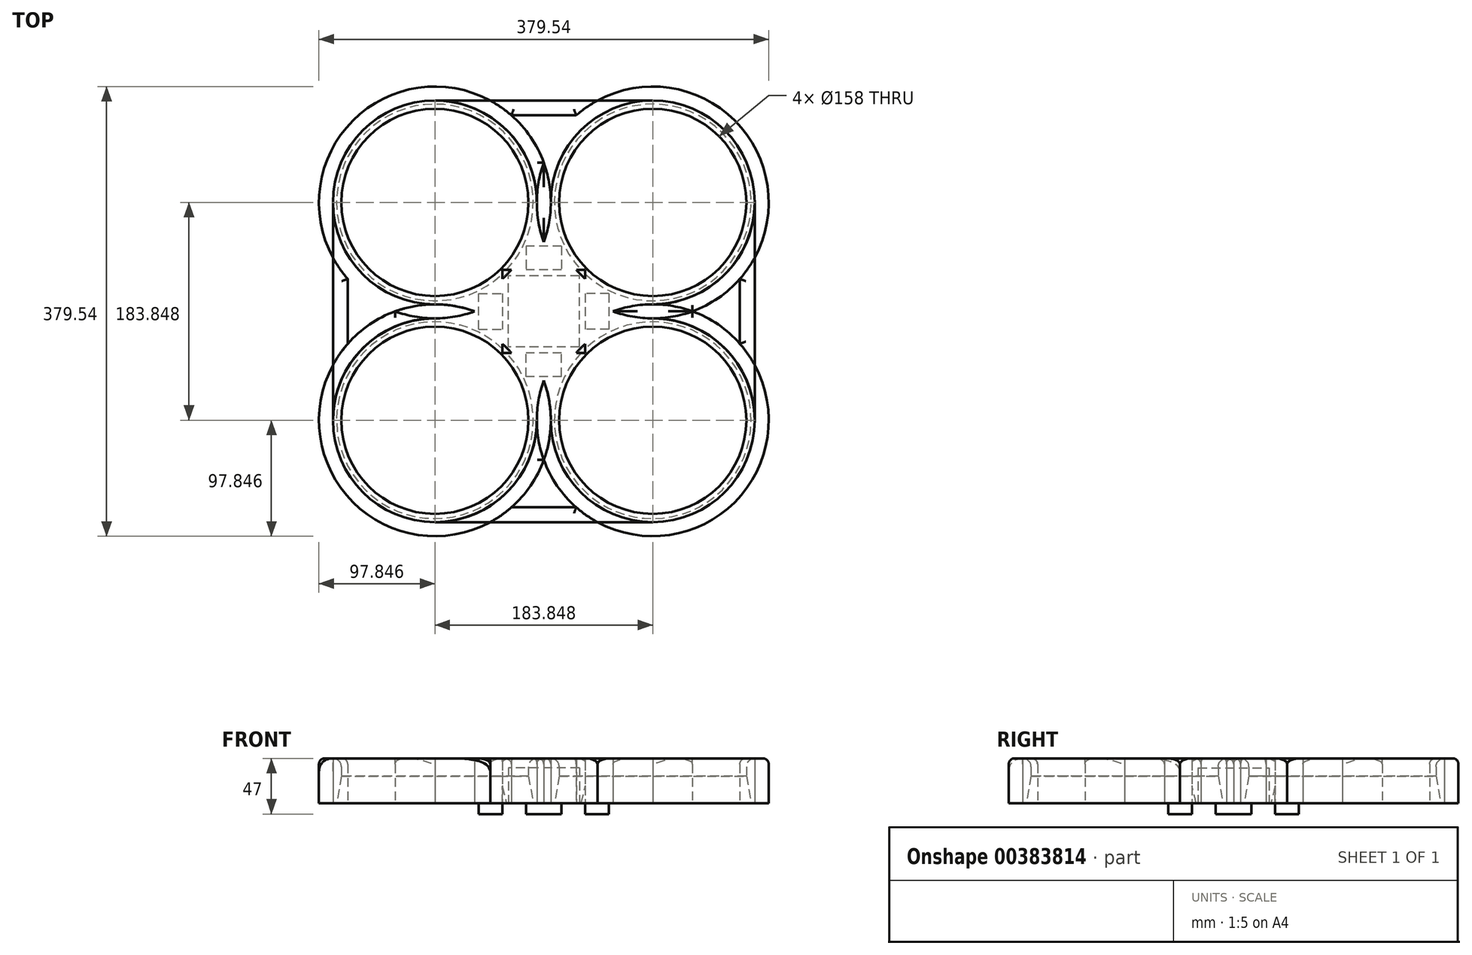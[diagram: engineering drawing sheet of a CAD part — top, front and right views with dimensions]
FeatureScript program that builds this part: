
annotation { "Feature Type Name" : "Feature", "Feature Type Description" : "" }
export const myFeature = defineFeature(function(context is Context, id is Id, definition is map)
    precondition{}
    {
        {
            var Q0;
            Q0=qCreatedBy(makeId("Top.planeOp"),FACE);
            var sketch = newSketch(context, id + "F0", { "sketchPlane" : qUnion([Q0])});
            skLineSegment(sketch, "E0.bottom", {"start": v(35, 35) * mm, "end": v(-35, 35) * mm});
            skLineSegment(sketch, "E0.top", {"start": v(35, -35) * mm, "end": v(-35, -35) * mm});
            skLineSegment(sketch, "E0.left", {"start": v(35, 35) * mm, "end": v(35, -35) * mm});
            skLineSegment(sketch, "E0.right", {"start": v(-35, 35) * mm, "end": v(-35, -35) * mm});
            skPoint(sketch, "E0.middle", {"position": v(0, 0) * mm});
            skLineSegment(sketch, "E1", {"start": v(0, 0) * mm, "end": v(91.92, 91.92) * mm, "construction": true});
            skLineSegment(sketch, "E2", {"start": v(0, 0) * mm, "end": v(-91.92, 91.92) * mm, "construction": true});
            skLineSegment(sketch, "E3", {"start": v(0, 0) * mm, "end": v(91.92, -91.92) * mm, "construction": true});
            skLineSegment(sketch, "E4", {"start": v(0, 0) * mm, "end": v(-91.92, -91.92) * mm, "construction": true});
            skCircle(sketch, "E5", {"center": v(-91.92, 91.92) * mm, "radius": 76.2 * mm, "construction": true});
            skCircle(sketch, "E6", {"center": v(-91.92, -91.92) * mm, "radius": 76.2 * mm, "construction": true});
            skCircle(sketch, "E7", {"center": v(91.92, -91.92) * mm, "radius": 76.2 * mm, "construction": true});
            skCircle(sketch, "E8", {"center": v(91.92, 91.92) * mm, "radius": 76.2 * mm, "construction": true});
            skCircle(sketch, "E9", {"center": v(-91.92, 91.92) * mm, "radius": 79 * mm});
            skCircle(sketch, "E10", {"center": v(91.92, 91.92) * mm, "radius": 79 * mm});
            skCircle(sketch, "E11", {"center": v(91.92, -91.92) * mm, "radius": 79 * mm});
            skCircle(sketch, "E12", {"center": v(-91.92, -91.92) * mm, "radius": 79 * mm});
            skCircle(sketch, "E13", {"center": v(91.92, -91.92) * mm, "radius": 86 * mm});
            skCircle(sketch, "E14", {"center": v(-91.92, -91.92) * mm, "radius": 86 * mm});
            skCircle(sketch, "E15", {"center": v(91.92, 91.92) * mm, "radius": 86 * mm});
            skCircle(sketch, "E16", {"center": v(-91.92, 91.92) * mm, "radius": 86 * mm});
            skLineSegment(sketch, "E17", {"start": v(-91.92, 91.92) * mm, "end": v(-177.92, 91.92) * mm, "construction": true});
            skLineSegment(sketch, "E18", {"start": v(-177.92, 91.92) * mm, "end": v(-177.92, -91.92) * mm});
            skLineSegment(sketch, "E19", {"start": v(-91.92, -91.92) * mm, "end": v(-91.92, -177.92) * mm, "construction": true});
            skLineSegment(sketch, "E20", {"start": v(-91.92, -177.92) * mm, "end": v(91.92, -177.92) * mm});
            skLineSegment(sketch, "E21", {"start": v(91.92, -91.92) * mm, "end": v(177.92, -91.92) * mm, "construction": true});
            skLineSegment(sketch, "E22", {"start": v(177.92, -91.92) * mm, "end": v(177.92, 91.92) * mm});
            skLineSegment(sketch, "E23", {"start": v(91.92, 91.92) * mm, "end": v(91.92, 177.92) * mm, "construction": true});
            skLineSegment(sketch, "E24", {"start": v(91.92, 177.92) * mm, "end": v(-91.92, 177.92) * mm});
            skCircle(sketch, "E25", {"center": v(-91.92, -91.92) * mm, "radius": 97.85 * mm});
            skCircle(sketch, "E26", {"center": v(-91.92, 91.92) * mm, "radius": 97.85 * mm});
            skLineSegment(sketch, "E27", {"start": v(0, 0) * mm, "end": v(-125.45, 0) * mm, "construction": true});
            skLineSegment(sketch, "E28", {"start": v(-125.45, 0) * mm, "end": v(-165.45, 0) * mm, "construction": true});
            skLineSegment(sketch, "E29", {"start": v(-165.45, 0) * mm, "end": v(-165.45, 27.37) * mm});
            skLineSegment(sketch, "E30", {"start": v(-165.45, 27.37) * mm, "end": v(-165.45, -27.37) * mm});
            skCircle(sketch, "E31", {"center": v(91.92, -91.92) * mm, "radius": 97.85 * mm});
            skCircle(sketch, "E32", {"center": v(91.92, 91.92) * mm, "radius": 97.85 * mm});
            skLineSegment(sketch, "E33", {"start": v(0, 0) * mm, "end": v(0, 125.45) * mm, "construction": true});
            skLineSegment(sketch, "E34", {"start": v(0, 125.45) * mm, "end": v(0, 165.45) * mm, "construction": true});
            skLineSegment(sketch, "E35", {"start": v(0, 165.45) * mm, "end": v(27.37, 165.45) * mm});
            skLineSegment(sketch, "E36", {"start": v(27.37, 165.45) * mm, "end": v(-27.37, 165.45) * mm});
            skLineSegment(sketch, "E37", {"start": v(0, 0) * mm, "end": v(0, -125.45) * mm, "construction": true});
            skLineSegment(sketch, "E38", {"start": v(0, -125.45) * mm, "end": v(0, -165.45) * mm, "construction": true});
            skLineSegment(sketch, "E39", {"start": v(0, -165.45) * mm, "end": v(27.37, -165.45) * mm});
            skLineSegment(sketch, "E40", {"start": v(27.37, -165.45) * mm, "end": v(-27.37, -165.45) * mm});
            skLineSegment(sketch, "E41", {"start": v(0, 0) * mm, "end": v(125.45, 0) * mm, "construction": true});
            skLineSegment(sketch, "E42", {"start": v(125.45, 0) * mm, "end": v(165.45, 0) * mm, "construction": true});
            skLineSegment(sketch, "E43", {"start": v(165.45, 0) * mm, "end": v(165.45, 27.37) * mm});
            skLineSegment(sketch, "E44", {"start": v(165.45, 27.37) * mm, "end": v(165.45, -27.37) * mm});
            skSolve(sketch);
        }
        {
            var Q0;
            {var subQ0=sQuery(id+"F0.wireOp",EDGE,"E20");var subQ1=sQuery(id+"F0.wireOp",EDGE,"E13");var subQ2=makeQuery(id+"F0.imprint","INTERSECT",VERTEX,{"derivedFrom":[subQ1,subQ0]});Q0=makeQuery(id+"F0.imprint","IMPRINT",FACE,{"disambiguationData":[TD([[makeQuery(id+"F0.imprint","IMPRINT",EDGE,{"disambiguationData":[TD([[subQ2,1.0]])],"derivedFrom":subQ1}),-1.0]])]});}
            var Q1;
            {var subQ0=sQuery(id+"F0.wireOp",EDGE,"E24");var subQ3=sQuery(id+"F0.wireOp",EDGE,"E26");var subQ5=makeQuery(id+"F0.imprint","INTERSECT",VERTEX,{"derivedFrom":[subQ0,subQ3]});Q1=makeQuery(id+"F0.imprint","IMPRINT",FACE,{"disambiguationData":[TD([[makeQuery(id+"F0.imprint","IMPRINT",EDGE,{"disambiguationData":[TD([[subQ5,1.0]])],"derivedFrom":subQ3}),-1.0]])]});}
            var Q2;
            {var subQ5=sQuery(id+"F0.wireOp",EDGE,"E22");Q2=makeQuery(id+"F0.imprint","IMPRINT",FACE,{"disambiguationData":[TD([[makeQuery(id+"F0.imprint","IMPRINT",EDGE,{"derivedFrom":subQ5}),1.0]])]});}
            var Q3;
            {var subQ4=sQuery(id+"F0.wireOp",EDGE,"E10");var subQ5=sQuery(id+"F0.wireOp",EDGE,"E1");var subQ6=makeQuery(id+"F0.imprint","INTERSECT",VERTEX,{"derivedFrom":[subQ5,subQ4]});Q3=makeQuery(id+"F0.imprint","IMPRINT",FACE,{"disambiguationData":[TD([[makeQuery(id+"F0.imprint","IMPRINT",EDGE,{"disambiguationData":[TD([[subQ6,-1.0]])],"derivedFrom":subQ4}),-1.0]])]});}
            var Q4;
            {var subQ0=sQuery(id+"F0.wireOp",EDGE,"E11");var subQ1=sQuery(id+"F0.wireOp",EDGE,"E3");var subQ2=makeQuery(id+"F0.imprint","INTERSECT",VERTEX,{"derivedFrom":[subQ1,subQ0]});Q4=makeQuery(id+"F0.imprint","IMPRINT",FACE,{"disambiguationData":[TD([[makeQuery(id+"F0.imprint","IMPRINT",EDGE,{"disambiguationData":[TD([[subQ2,1.0]])],"derivedFrom":subQ0}),-1.0]])]});}
            var Q5;
            {var subQ1=sQuery(id+"F0.wireOp",EDGE,"E26");var subQ3=sQuery(id+"F0.wireOp",EDGE,"E18");var subQ4=makeQuery(id+"F0.imprint","INTERSECT",VERTEX,{"derivedFrom":[subQ3,subQ1]});Q5=makeQuery(id+"F0.imprint","IMPRINT",FACE,{"disambiguationData":[TD([[makeQuery(id+"F0.imprint","IMPRINT",EDGE,{"disambiguationData":[TD([[subQ4,-1.0]])],"derivedFrom":subQ3}),1.0]])]});}
            var Q6;
            {var subQ4=sQuery(id+"F0.wireOp",EDGE,"E10");var subQ5=sQuery(id+"F0.wireOp",EDGE,"E1");var subQ6=makeQuery(id+"F0.imprint","INTERSECT",VERTEX,{"derivedFrom":[subQ5,subQ4]});Q6=makeQuery(id+"F0.imprint","IMPRINT",FACE,{"disambiguationData":[TD([[makeQuery(id+"F0.imprint","IMPRINT",EDGE,{"disambiguationData":[TD([[subQ6,1.0]])],"derivedFrom":subQ4}),-1.0]])]});}
            var Q7;
            {var subQ0=sQuery(id+"F0.wireOp",EDGE,"E26");var subQ6=sQuery(id+"F0.wireOp",EDGE,"E0.bottom");var subQ8=makeQuery(id+"F0.imprint","INTERSECT",VERTEX,{"derivedFrom":[subQ6,subQ0]});Q7=makeQuery(id+"F0.imprint","IMPRINT",FACE,{"disambiguationData":[TD([[makeQuery(id+"F0.imprint","IMPRINT",EDGE,{"disambiguationData":[TD([[subQ8,-1.0]])],"derivedFrom":subQ6}),-1.0]])]});}
            var Q8;
            {var subQ4=sQuery(id+"F0.wireOp",EDGE,"E11");var subQ5=sQuery(id+"F0.wireOp",EDGE,"E3");var subQ6=makeQuery(id+"F0.imprint","INTERSECT",VERTEX,{"derivedFrom":[subQ5,subQ4]});Q8=makeQuery(id+"F0.imprint","IMPRINT",FACE,{"disambiguationData":[TD([[makeQuery(id+"F0.imprint","IMPRINT",EDGE,{"disambiguationData":[TD([[subQ6,-1.0]])],"derivedFrom":subQ4}),-1.0]])]});}
            var Q9;
            {var subQ0=sQuery(id+"F0.wireOp",EDGE,"E25");var subQ1=sQuery(id+"F0.wireOp",EDGE,"E0.top");var subQ2=makeQuery(id+"F0.imprint","INTERSECT",VERTEX,{"derivedFrom":[subQ1,subQ0]});Q9=makeQuery(id+"F0.imprint","IMPRINT",FACE,{"disambiguationData":[TD([[makeQuery(id+"F0.imprint","IMPRINT",EDGE,{"disambiguationData":[TD([[subQ2,-1.0]])],"derivedFrom":subQ1}),1.0]])]});}
            var Q10;
            {var subQ2=sQuery(id+"F0.wireOp",EDGE,"E18");var subQ4=sQuery(id+"F0.wireOp",EDGE,"E14");var subQ5=makeQuery(id+"F0.imprint","INTERSECT",VERTEX,{"derivedFrom":[subQ4,subQ2]});Q10=makeQuery(id+"F0.imprint","IMPRINT",FACE,{"disambiguationData":[TD([[makeQuery(id+"F0.imprint","IMPRINT",EDGE,{"disambiguationData":[TD([[subQ5,1.0]])],"derivedFrom":subQ4}),-1.0]])]});}
            var Q11;
            {var subQ0=sQuery(id+"F0.wireOp",EDGE,"E26");var subQ1=makeQuery(id+"F0.imprint","INTERSECT",VERTEX,{"derivedFrom":[subQ0,sQuery(id+"F0.wireOp",EDGE,"E30")]});Q11=makeQuery(id+"F0.imprint","IMPRINT",FACE,{"disambiguationData":[TD([[makeQuery(id+"F0.imprint","IMPRINT",EDGE,{"disambiguationData":[TD([[subQ1,1.0]])],"derivedFrom":subQ0}),1.0]])]});}
            var Q12;
            {var subQ4=sQuery(id+"F0.wireOp",EDGE,"E12");var subQ5=sQuery(id+"F0.wireOp",EDGE,"E4");var subQ6=makeQuery(id+"F0.imprint","INTERSECT",VERTEX,{"derivedFrom":[subQ5,subQ4]});Q12=makeQuery(id+"F0.imprint","IMPRINT",FACE,{"disambiguationData":[TD([[makeQuery(id+"F0.imprint","IMPRINT",EDGE,{"disambiguationData":[TD([[subQ6,-1.0]])],"derivedFrom":subQ4}),-1.0]])]});}
            var Q13;
            {var subQ0=sQuery(id+"F0.wireOp",EDGE,"E2");var subQ3=sQuery(id+"F0.wireOp",EDGE,"E9");var subQ4=makeQuery(id+"F0.imprint","INTERSECT",VERTEX,{"derivedFrom":[subQ0,subQ3]});Q13=makeQuery(id+"F0.imprint","IMPRINT",FACE,{"disambiguationData":[TD([[makeQuery(id+"F0.imprint","IMPRINT",EDGE,{"disambiguationData":[TD([[subQ4,-1.0]])],"derivedFrom":subQ3}),-1.0]])]});}
            var Q14;
            {var subQ4=sQuery(id+"F0.wireOp",EDGE,"E9");var subQ5=sQuery(id+"F0.wireOp",EDGE,"E2");var subQ6=makeQuery(id+"F0.imprint","INTERSECT",VERTEX,{"derivedFrom":[subQ5,subQ4]});Q14=makeQuery(id+"F0.imprint","IMPRINT",FACE,{"disambiguationData":[TD([[makeQuery(id+"F0.imprint","IMPRINT",EDGE,{"disambiguationData":[TD([[subQ6,1.0]])],"derivedFrom":subQ4}),-1.0]])]});}
            var Q15;
            {var subQ0=sQuery(id+"F0.wireOp",EDGE,"E25");var subQ1=makeQuery(id+"F0.imprint","INTERSECT",VERTEX,{"derivedFrom":[sQuery(id+"F0.wireOp",EDGE,"E16"),subQ0]});Q15=makeQuery(id+"F0.imprint","IMPRINT",FACE,{"disambiguationData":[TD([[makeQuery(id+"F0.imprint","IMPRINT",EDGE,{"disambiguationData":[TD([[subQ1,1.0]])],"derivedFrom":subQ0}),1.0]])]});}
            var Q16;
            {var subQ1=sQuery(id+"F0.wireOp",EDGE,"E26");var subQ4=makeQuery(id+"F0.imprint","INTERSECT",VERTEX,{"derivedFrom":[sQuery(id+"F0.wireOp",EDGE,"E14"),subQ1]});Q16=makeQuery(id+"F0.imprint","IMPRINT",FACE,{"disambiguationData":[TD([[makeQuery(id+"F0.imprint","IMPRINT",EDGE,{"disambiguationData":[TD([[subQ4,-1.0]])],"derivedFrom":subQ1}),1.0]])]});}
            var Q17;
            {var subQ0=sQuery(id+"F0.wireOp",EDGE,"E25");var subQ1=sQuery(id+"F0.wireOp",EDGE,"E0.right");var subQ2=makeQuery(id+"F0.imprint","INTERSECT",VERTEX,{"derivedFrom":[subQ1,subQ0]});Q17=makeQuery(id+"F0.imprint","IMPRINT",FACE,{"disambiguationData":[TD([[makeQuery(id+"F0.imprint","IMPRINT",EDGE,{"disambiguationData":[TD([[subQ2,-1.0]])],"derivedFrom":subQ1}),-1.0]])]});}
            var Q18;
            {var subQ0=sQuery(id+"F0.wireOp",EDGE,"E16");var subQ1=sQuery(id+"F0.wireOp",EDGE,"E0.right");var subQ2=makeQuery(id+"F0.imprint","INTERSECT",VERTEX,{"derivedFrom":[subQ1,subQ0]});Q18=makeQuery(id+"F0.imprint","IMPRINT",FACE,{"disambiguationData":[TD([[makeQuery(id+"F0.imprint","IMPRINT",EDGE,{"disambiguationData":[TD([[subQ2,-1.0]])],"derivedFrom":subQ1}),-1.0]])]});}
            var Q19;
            {var subQ1=sQuery(id+"F0.wireOp",EDGE,"E0.right");var subQ3=sQuery(id+"F0.wireOp",EDGE,"E16");var subQ4=makeQuery(id+"F0.imprint","INTERSECT",VERTEX,{"derivedFrom":[subQ1,subQ3]});Q19=makeQuery(id+"F0.imprint","IMPRINT",FACE,{"disambiguationData":[TD([[makeQuery(id+"F0.imprint","IMPRINT",EDGE,{"disambiguationData":[TD([[subQ4,-1.0]])],"derivedFrom":subQ3}),1.0]])]});}
            var Q20;
            {var subQ1=sQuery(id+"F0.wireOp",EDGE,"E0.bottom");var subQ3=sQuery(id+"F0.wireOp",EDGE,"E16");var subQ4=makeQuery(id+"F0.imprint","INTERSECT",VERTEX,{"derivedFrom":[subQ1,subQ3]});Q20=makeQuery(id+"F0.imprint","IMPRINT",FACE,{"disambiguationData":[TD([[makeQuery(id+"F0.imprint","IMPRINT",EDGE,{"disambiguationData":[TD([[subQ4,1.0]])],"derivedFrom":subQ3}),1.0]])]});}
            var Q21;
            {var subQ1=sQuery(id+"F0.wireOp",EDGE,"E0.right");var subQ3=sQuery(id+"F0.wireOp",EDGE,"E14");var subQ4=makeQuery(id+"F0.imprint","INTERSECT",VERTEX,{"derivedFrom":[subQ1,subQ3]});Q21=makeQuery(id+"F0.imprint","IMPRINT",FACE,{"disambiguationData":[TD([[makeQuery(id+"F0.imprint","IMPRINT",EDGE,{"disambiguationData":[TD([[subQ4,1.0]])],"derivedFrom":subQ3}),1.0]])]});}
            var Q22;
            {var subQ0=sQuery(id+"F0.wireOp",EDGE,"E12");var subQ1=sQuery(id+"F0.wireOp",EDGE,"E4");var subQ2=makeQuery(id+"F0.imprint","INTERSECT",VERTEX,{"derivedFrom":[subQ1,subQ0]});Q22=makeQuery(id+"F0.imprint","IMPRINT",FACE,{"disambiguationData":[TD([[makeQuery(id+"F0.imprint","IMPRINT",EDGE,{"disambiguationData":[TD([[subQ2,1.0]])],"derivedFrom":subQ0}),-1.0]])]});}
            var Q23;
            {var subQ0=sQuery(id+"F0.wireOp",EDGE,"E26");var subQ1=sQuery(id+"F0.wireOp",EDGE,"E0.right");var subQ2=makeQuery(id+"F0.imprint","INTERSECT",VERTEX,{"derivedFrom":[subQ1,subQ0]});Q23=makeQuery(id+"F0.imprint","IMPRINT",FACE,{"disambiguationData":[TD([[makeQuery(id+"F0.imprint","IMPRINT",EDGE,{"disambiguationData":[TD([[subQ2,-1.0]])],"derivedFrom":subQ1}),-1.0]])]});}
            var Q24;
            {var subQ0=sQuery(id+"F0.wireOp",EDGE,"E27");var subQ1=sQuery(id+"F0.wireOp",EDGE,"E0.right");var subQ2=makeQuery(id+"F0.imprint","INTERSECT",VERTEX,{"derivedFrom":[subQ1,subQ0]});Q24=makeQuery(id+"F0.imprint","IMPRINT",FACE,{"disambiguationData":[TD([[makeQuery(id+"F0.imprint","IMPRINT",EDGE,{"disambiguationData":[TD([[subQ2,-1.0]])],"derivedFrom":subQ1}),-1.0]])]});}
            var Q25;
            {var subQ0=sQuery(id+"F0.wireOp",EDGE,"E13");var subQ1=sQuery(id+"F0.wireOp",EDGE,"E0.top");var subQ2=makeQuery(id+"F0.imprint","INTERSECT",VERTEX,{"derivedFrom":[subQ1,subQ0]});Q25=makeQuery(id+"F0.imprint","IMPRINT",FACE,{"disambiguationData":[TD([[makeQuery(id+"F0.imprint","IMPRINT",EDGE,{"disambiguationData":[TD([[subQ2,-1.0]])],"derivedFrom":subQ1}),1.0]])]});}
            var Q26;
            {var subQ0=sQuery(id+"F0.wireOp",EDGE,"E15");var subQ1=sQuery(id+"F0.wireOp",EDGE,"E0.bottom");var subQ2=makeQuery(id+"F0.imprint","INTERSECT",VERTEX,{"derivedFrom":[subQ1,subQ0]});Q26=makeQuery(id+"F0.imprint","IMPRINT",FACE,{"disambiguationData":[TD([[makeQuery(id+"F0.imprint","IMPRINT",EDGE,{"disambiguationData":[TD([[subQ2,-1.0]])],"derivedFrom":subQ1}),-1.0]])]});}
            var Q27;
            {var subQ0=sQuery(id+"F0.wireOp",EDGE,"E25");var subQ1=makeQuery(id+"F0.imprint","INTERSECT",VERTEX,{"derivedFrom":[sQuery(id+"F0.wireOp",EDGE,"E13"),subQ0]});Q27=makeQuery(id+"F0.imprint","IMPRINT",FACE,{"disambiguationData":[TD([[makeQuery(id+"F0.imprint","IMPRINT",EDGE,{"disambiguationData":[TD([[subQ1,-1.0]])],"derivedFrom":subQ0}),1.0]])]});}
            var Q28;
            {var subQ0=sQuery(id+"F0.wireOp",EDGE,"E31");var subQ1=makeQuery(id+"F0.imprint","INTERSECT",VERTEX,{"derivedFrom":[sQuery(id+"F0.wireOp",EDGE,"E14"),subQ0]});Q28=makeQuery(id+"F0.imprint","IMPRINT",FACE,{"disambiguationData":[TD([[makeQuery(id+"F0.imprint","IMPRINT",EDGE,{"disambiguationData":[TD([[subQ1,1.0]])],"derivedFrom":subQ0}),1.0]])]});}
            var Q29;
            {var subQ0=sQuery(id+"F0.wireOp",EDGE,"E25");var subQ1=makeQuery(id+"F0.imprint","INTERSECT",VERTEX,{"derivedFrom":[subQ0,sQuery(id+"F0.wireOp",EDGE,"E40")]});Q29=makeQuery(id+"F0.imprint","IMPRINT",FACE,{"disambiguationData":[TD([[makeQuery(id+"F0.imprint","IMPRINT",EDGE,{"disambiguationData":[TD([[subQ1,1.0]])],"derivedFrom":subQ0}),1.0]])]});}
            var Q30;
            {var subQ4=sQuery(id+"F0.wireOp",EDGE,"E20");var subQ6=sQuery(id+"F0.wireOp",EDGE,"E25");var subQ8=makeQuery(id+"F0.imprint","INTERSECT",VERTEX,{"derivedFrom":[subQ4,subQ6]});Q30=makeQuery(id+"F0.imprint","IMPRINT",FACE,{"disambiguationData":[TD([[makeQuery(id+"F0.imprint","IMPRINT",EDGE,{"disambiguationData":[TD([[subQ8,-1.0]])],"derivedFrom":subQ4}),1.0]])]});}
            var Q31;
            {var subQ2=sQuery(id+"F0.wireOp",EDGE,"E24");var subQ6=sQuery(id+"F0.wireOp",EDGE,"E16");var subQ8=makeQuery(id+"F0.imprint","INTERSECT",VERTEX,{"derivedFrom":[subQ6,subQ2]});Q31=makeQuery(id+"F0.imprint","IMPRINT",FACE,{"disambiguationData":[TD([[makeQuery(id+"F0.imprint","IMPRINT",EDGE,{"disambiguationData":[TD([[subQ8,1.0]])],"derivedFrom":subQ6}),-1.0]])]});}
            var Q32;
            {var subQ0=sQuery(id+"F0.wireOp",EDGE,"E32");var subQ1=makeQuery(id+"F0.imprint","INTERSECT",VERTEX,{"derivedFrom":[subQ0,sQuery(id+"F0.wireOp",EDGE,"E36")]});Q32=makeQuery(id+"F0.imprint","IMPRINT",FACE,{"disambiguationData":[TD([[makeQuery(id+"F0.imprint","IMPRINT",EDGE,{"disambiguationData":[TD([[subQ1,1.0]])],"derivedFrom":subQ0}),1.0]])]});}
            var Q33;
            {var subQ1=sQuery(id+"F0.wireOp",EDGE,"E32");var subQ4=makeQuery(id+"F0.imprint","INTERSECT",VERTEX,{"derivedFrom":[sQuery(id+"F0.wireOp",EDGE,"E16"),subQ1]});Q33=makeQuery(id+"F0.imprint","IMPRINT",FACE,{"disambiguationData":[TD([[makeQuery(id+"F0.imprint","IMPRINT",EDGE,{"disambiguationData":[TD([[subQ4,-1.0]])],"derivedFrom":subQ1}),1.0]])]});}
            var Q34;
            {var subQ2=sQuery(id+"F0.wireOp",EDGE,"E26");var subQ4=makeQuery(id+"F0.imprint","INTERSECT",VERTEX,{"derivedFrom":[sQuery(id+"F0.wireOp",EDGE,"E15"),subQ2]});Q34=makeQuery(id+"F0.imprint","IMPRINT",FACE,{"disambiguationData":[TD([[makeQuery(id+"F0.imprint","IMPRINT",EDGE,{"disambiguationData":[TD([[subQ4,1.0]])],"derivedFrom":subQ2}),1.0]])]});}
            var Q35;
            {var subQ0=sQuery(id+"F0.wireOp",EDGE,"E15");var subQ1=sQuery(id+"F0.wireOp",EDGE,"E0.left");var subQ2=makeQuery(id+"F0.imprint","INTERSECT",VERTEX,{"derivedFrom":[subQ1,subQ0]});Q35=makeQuery(id+"F0.imprint","IMPRINT",FACE,{"disambiguationData":[TD([[makeQuery(id+"F0.imprint","IMPRINT",EDGE,{"disambiguationData":[TD([[subQ2,-1.0]])],"derivedFrom":subQ1}),1.0]])]});}
            var Q36;
            {var subQ0=sQuery(id+"F0.wireOp",EDGE,"E32");var subQ1=makeQuery(id+"F0.imprint","INTERSECT",VERTEX,{"derivedFrom":[sQuery(id+"F0.wireOp",EDGE,"E13"),subQ0]});Q36=makeQuery(id+"F0.imprint","IMPRINT",FACE,{"disambiguationData":[TD([[makeQuery(id+"F0.imprint","IMPRINT",EDGE,{"disambiguationData":[TD([[subQ1,1.0]])],"derivedFrom":subQ0}),1.0]])]});}
            var Q37;
            {var subQ2=sQuery(id+"F0.wireOp",EDGE,"E31");var subQ4=makeQuery(id+"F0.imprint","INTERSECT",VERTEX,{"derivedFrom":[sQuery(id+"F0.wireOp",EDGE,"E15"),subQ2]});Q37=makeQuery(id+"F0.imprint","IMPRINT",FACE,{"disambiguationData":[TD([[makeQuery(id+"F0.imprint","IMPRINT",EDGE,{"disambiguationData":[TD([[subQ4,-1.0]])],"derivedFrom":subQ2}),1.0]])]});}
            var Q38;
            {var subQ0=sQuery(id+"F0.wireOp",EDGE,"E31");var subQ1=sQuery(id+"F0.wireOp",EDGE,"E0.left");var subQ2=makeQuery(id+"F0.imprint","INTERSECT",VERTEX,{"derivedFrom":[subQ1,subQ0]});Q38=makeQuery(id+"F0.imprint","IMPRINT",FACE,{"disambiguationData":[TD([[makeQuery(id+"F0.imprint","IMPRINT",EDGE,{"disambiguationData":[TD([[subQ2,-1.0]])],"derivedFrom":subQ1}),1.0]])]});}
            var Q39;
            {var subQ1=sQuery(id+"F0.wireOp",EDGE,"E0.top");var subQ3=sQuery(id+"F0.wireOp",EDGE,"E14");var subQ4=makeQuery(id+"F0.imprint","INTERSECT",VERTEX,{"derivedFrom":[subQ1,subQ3]});Q39=makeQuery(id+"F0.imprint","IMPRINT",FACE,{"disambiguationData":[TD([[makeQuery(id+"F0.imprint","IMPRINT",EDGE,{"disambiguationData":[TD([[subQ4,-1.0]])],"derivedFrom":subQ3}),1.0]])]});}
            var Q40;
            {var subQ0=sQuery(id+"F0.wireOp",EDGE,"E32");var subQ1=sQuery(id+"F0.wireOp",EDGE,"E0.bottom");var subQ2=makeQuery(id+"F0.imprint","INTERSECT",VERTEX,{"derivedFrom":[subQ1,subQ0]});Q40=makeQuery(id+"F0.imprint","IMPRINT",FACE,{"disambiguationData":[TD([[makeQuery(id+"F0.imprint","IMPRINT",EDGE,{"disambiguationData":[TD([[subQ2,-1.0]])],"derivedFrom":subQ1}),-1.0]])]});}
            var Q41;
            {var subQ0=sQuery(id+"F0.wireOp",EDGE,"E33");var subQ1=sQuery(id+"F0.wireOp",EDGE,"E0.bottom");var subQ2=makeQuery(id+"F0.imprint","INTERSECT",VERTEX,{"derivedFrom":[subQ1,subQ0]});Q41=makeQuery(id+"F0.imprint","IMPRINT",FACE,{"disambiguationData":[TD([[makeQuery(id+"F0.imprint","IMPRINT",EDGE,{"disambiguationData":[TD([[subQ2,-1.0]])],"derivedFrom":subQ1}),-1.0]])]});}
            var Q42;
            {var subQ0=sQuery(id+"F0.wireOp",EDGE,"E41");var subQ1=sQuery(id+"F0.wireOp",EDGE,"E0.left");var subQ2=makeQuery(id+"F0.imprint","INTERSECT",VERTEX,{"derivedFrom":[subQ1,subQ0]});Q42=makeQuery(id+"F0.imprint","IMPRINT",FACE,{"disambiguationData":[TD([[makeQuery(id+"F0.imprint","IMPRINT",EDGE,{"disambiguationData":[TD([[subQ2,-1.0]])],"derivedFrom":subQ1}),1.0]])]});}
            var Q43;
            {var subQ0=sQuery(id+"F0.wireOp",EDGE,"E32");var subQ1=sQuery(id+"F0.wireOp",EDGE,"E0.left");var subQ2=makeQuery(id+"F0.imprint","INTERSECT",VERTEX,{"derivedFrom":[subQ1,subQ0]});Q43=makeQuery(id+"F0.imprint","IMPRINT",FACE,{"disambiguationData":[TD([[makeQuery(id+"F0.imprint","IMPRINT",EDGE,{"disambiguationData":[TD([[subQ2,-1.0]])],"derivedFrom":subQ1}),1.0]])]});}
            var Q44;
            Q44=makeQuery(id+"F0.imprint","IMPRINT",FACE,{"disambiguationData":[TD([[makeQuery(id+"F0.imprint","IMPRINT",EDGE,{"derivedFrom":sQuery(id+"F0.wireOp",EDGE,"E12")}),-1.0]])]});
            var Q45;
            Q45=makeQuery(id+"F0.imprint","IMPRINT",FACE,{"disambiguationData":[TD([[makeQuery(id+"F0.imprint","IMPRINT",EDGE,{"derivedFrom":sQuery(id+"F0.wireOp",EDGE,"E11")}),-1.0]])]});
            var Q46;
            Q46=makeQuery(id+"F0.imprint","IMPRINT",FACE,{"disambiguationData":[TD([[makeQuery(id+"F0.imprint","IMPRINT",EDGE,{"derivedFrom":sQuery(id+"F0.wireOp",EDGE,"E10")}),-1.0]])]});
            var Q47;
            Q47=makeQuery(id+"F0.imprint","IMPRINT",FACE,{"disambiguationData":[TD([[makeQuery(id+"F0.imprint","IMPRINT",EDGE,{"derivedFrom":sQuery(id+"F0.wireOp",EDGE,"E9")}),-1.0]])]});
            var Q48;
            {var subQ5=sQuery(id+"F0.wireOp",EDGE,"E32");var subQ13=sQuery(id+"F0.wireOp",EDGE,"E0.bottom");var subQ14=makeQuery(id+"F0.imprint","INTERSECT",VERTEX,{"derivedFrom":[subQ13,subQ5]});Q48=makeQuery(id+"F0.imprint","IMPRINT",FACE,{"disambiguationData":[TD([[makeQuery(id+"F0.imprint","IMPRINT",EDGE,{"disambiguationData":[TD([[subQ14,-1.0]])],"derivedFrom":subQ13}),1.0]])]});}
            var Q49;
            {var subQ0=sQuery(id+"F0.wireOp",EDGE,"E26");var subQ1=sQuery(id+"F0.wireOp",EDGE,"E0.bottom");var subQ2=makeQuery(id+"F0.imprint","INTERSECT",VERTEX,{"derivedFrom":[subQ1,subQ0]});Q49=makeQuery(id+"F0.imprint","IMPRINT",FACE,{"disambiguationData":[TD([[makeQuery(id+"F0.imprint","IMPRINT",EDGE,{"disambiguationData":[TD([[subQ2,-1.0]])],"derivedFrom":subQ1}),1.0]])]});}
            var Q50;
            {var subQ0=sQuery(id+"F0.wireOp",EDGE,"E15");var subQ1=sQuery(id+"F0.wireOp",EDGE,"E0.bottom");var subQ2=makeQuery(id+"F0.imprint","INTERSECT",VERTEX,{"derivedFrom":[subQ1,subQ0]});Q50=makeQuery(id+"F0.imprint","IMPRINT",FACE,{"disambiguationData":[TD([[makeQuery(id+"F0.imprint","IMPRINT",EDGE,{"disambiguationData":[TD([[subQ2,-1.0]])],"derivedFrom":subQ1}),1.0]])]});}
            var Q51;
            {var subQ0=sQuery(id+"F0.wireOp",EDGE,"E13");var subQ1=sQuery(id+"F0.wireOp",EDGE,"E0.top");var subQ2=makeQuery(id+"F0.imprint","INTERSECT",VERTEX,{"derivedFrom":[subQ1,subQ0]});Q51=makeQuery(id+"F0.imprint","IMPRINT",FACE,{"disambiguationData":[TD([[makeQuery(id+"F0.imprint","IMPRINT",EDGE,{"disambiguationData":[TD([[subQ2,-1.0]])],"derivedFrom":subQ1}),-1.0]])]});}
            var Q52;
            {var subQ0=sQuery(id+"F0.wireOp",EDGE,"E25");var subQ1=sQuery(id+"F0.wireOp",EDGE,"E0.top");var subQ2=makeQuery(id+"F0.imprint","INTERSECT",VERTEX,{"derivedFrom":[subQ1,subQ0]});Q52=makeQuery(id+"F0.imprint","IMPRINT",FACE,{"disambiguationData":[TD([[makeQuery(id+"F0.imprint","IMPRINT",EDGE,{"disambiguationData":[TD([[subQ2,-1.0]])],"derivedFrom":subQ1}),-1.0]])]});}
            var Q53;
            {var subQ0=sQuery(id+"F0.wireOp",EDGE,"E31");var subQ1=sQuery(id+"F0.wireOp",EDGE,"E0.top");var subQ2=makeQuery(id+"F0.imprint","INTERSECT",VERTEX,{"derivedFrom":[subQ1,subQ0]});Q53=makeQuery(id+"F0.imprint","IMPRINT",FACE,{"disambiguationData":[TD([[makeQuery(id+"F0.imprint","IMPRINT",EDGE,{"disambiguationData":[TD([[subQ2,-1.0]])],"derivedFrom":subQ1}),1.0]])]});}
            var Q54;
            {var subQ0=sQuery(id+"F0.wireOp",EDGE,"E0.left");var subQ1=sQuery(id+"F0.wireOp",EDGE,"E0.top");var subQ2=makeQuery(id+"F0.imprint","INTERSECT",VERTEX,{"derivedFrom":[subQ1,subQ0]});Q54=makeQuery(id+"F0.imprint","IMPRINT",FACE,{"disambiguationData":[TD([[makeQuery(id+"F0.imprint","IMPRINT",EDGE,{"disambiguationData":[TD([[subQ2,-1.0]])],"derivedFrom":subQ1}),-1.0]])]});}
            var Q55;
            {var subQ0=sQuery(id+"F0.wireOp",EDGE,"E0.left");var subQ1=sQuery(id+"F0.wireOp",EDGE,"E0.bottom");var subQ2=makeQuery(id+"F0.imprint","INTERSECT",VERTEX,{"derivedFrom":[subQ1,subQ0]});Q55=makeQuery(id+"F0.imprint","IMPRINT",FACE,{"disambiguationData":[TD([[makeQuery(id+"F0.imprint","IMPRINT",EDGE,{"disambiguationData":[TD([[subQ2,-1.0]])],"derivedFrom":subQ1}),1.0]])]});}
            var Q56;
            {var subQ0=sQuery(id+"F0.wireOp",EDGE,"E20");var subQ1=sQuery(id+"F0.wireOp",EDGE,"E13");var subQ2=makeQuery(id+"F0.imprint","INTERSECT",VERTEX,{"derivedFrom":[subQ1,subQ0]});Q56=makeQuery(id+"F0.imprint","IMPRINT",FACE,{"disambiguationData":[TD([[makeQuery(id+"F0.imprint","IMPRINT",EDGE,{"disambiguationData":[TD([[subQ2,-1.0]])],"derivedFrom":subQ1}),-1.0]])]});}
            var Q57;
            {var subQ0=sQuery(id+"F0.wireOp",EDGE,"E22");var subQ1=sQuery(id+"F0.wireOp",EDGE,"E15");var subQ2=makeQuery(id+"F0.imprint","INTERSECT",VERTEX,{"derivedFrom":[subQ1,subQ0]});Q57=makeQuery(id+"F0.imprint","IMPRINT",FACE,{"disambiguationData":[TD([[makeQuery(id+"F0.imprint","IMPRINT",EDGE,{"disambiguationData":[TD([[subQ2,-1.0]])],"derivedFrom":subQ1}),-1.0]])]});}
            var Q58;
            {var subQ0=sQuery(id+"F0.wireOp",EDGE,"E18");var subQ1=sQuery(id+"F0.wireOp",EDGE,"E16");var subQ2=makeQuery(id+"F0.imprint","INTERSECT",VERTEX,{"derivedFrom":[subQ1,subQ0]});Q58=makeQuery(id+"F0.imprint","IMPRINT",FACE,{"disambiguationData":[TD([[makeQuery(id+"F0.imprint","IMPRINT",EDGE,{"disambiguationData":[TD([[subQ2,1.0]])],"derivedFrom":subQ1}),-1.0]])]});}
            var Q59;
            {var subQ0=sQuery(id+"F0.wireOp",EDGE,"E18");var subQ1=sQuery(id+"F0.wireOp",EDGE,"E14");var subQ2=makeQuery(id+"F0.imprint","INTERSECT",VERTEX,{"derivedFrom":[subQ1,subQ0]});Q59=makeQuery(id+"F0.imprint","IMPRINT",FACE,{"disambiguationData":[TD([[makeQuery(id+"F0.imprint","IMPRINT",EDGE,{"disambiguationData":[TD([[subQ2,-1.0]])],"derivedFrom":subQ1}),-1.0]])]});}
            extrude(context, id + "F1", {"entities" : qUnion([Q0, Q1, Q2, Q3, Q4, Q5, Q6, Q7, Q8, Q9, Q10, Q11, Q12, Q13, Q14, Q15, Q16, Q17, Q18, Q19, Q20, Q21, Q22, Q23, Q24, Q25, Q26, Q27, Q28, Q29, Q30, Q31, Q32, Q33, Q34, Q35, Q36, Q37, Q38, Q39, Q40, Q41, Q42, Q43, Q44, Q45, Q46, Q47, Q48, Q49, Q50, Q51, Q52, Q53, Q54, Q55, Q56, Q57, Q58, Q59]), "depth" : 38 * mm});
        }
        {
            var Q0;
            Q0=makeQuery(id+"F1.opExtrude","CAP_EDGE",EDGE,{"disambiguationData":[OSD([sQuery(id+"F0.wireOp",EDGE,"E12")])],"isStart":false});
            var Q1;
            Q1=makeQuery(id+"F1.opExtrude","CAP_EDGE",EDGE,{"disambiguationData":[OSD([sQuery(id+"F0.wireOp",EDGE,"E9")])],"isStart":false});
            var Q2;
            Q2=makeQuery(id+"F1.opExtrude","CAP_EDGE",EDGE,{"disambiguationData":[OSD([sQuery(id+"F0.wireOp",EDGE,"E10")])],"isStart":false});
            var Q3;
            Q3=makeQuery(id+"F1.opExtrude","CAP_EDGE",EDGE,{"disambiguationData":[OSD([sQuery(id+"F0.wireOp",EDGE,"E11")])],"isStart":false});
            fillet(context, id + "F2", {"entities" : qUnion([Q0, Q1, Q2, Q3]), "radius" : 7 * mm, "tangentPropagation" : true, "allowEdgeOverflow" : false});
        }
        {
            var Q0;
            Q0=makeQuery(id+"F1.opExtrude","CAP_EDGE",EDGE,{"disambiguationData":[OSD([sQuery(id+"F0.wireOp",EDGE,"E12")])],"isStart":true});
            var Q1;
            Q1=makeQuery(id+"F1.opExtrude","CAP_EDGE",EDGE,{"disambiguationData":[OSD([sQuery(id+"F0.wireOp",EDGE,"E11")])],"isStart":true});
            var Q2;
            Q2=makeQuery(id+"F1.opExtrude","CAP_EDGE",EDGE,{"disambiguationData":[OSD([sQuery(id+"F0.wireOp",EDGE,"E10")])],"isStart":true});
            var Q3;
            Q3=makeQuery(id+"F1.opExtrude","CAP_EDGE",EDGE,{"disambiguationData":[OSD([sQuery(id+"F0.wireOp",EDGE,"E9")])],"isStart":true});
            chamfer(context, id + "F3", {"entities" : qUnion([Q0, Q1, Q2, Q3]), "chamferType" : ChamferType.TWO_OFFSETS, "width1" : 23 * mm, "oppositeDirection" : true, "width2" : 4 * mm, "tangentPropagation" : true});
        }
        {
            var Q0;
            Q0=qCreatedBy(makeId("Top.planeOp"),FACE);
            var sketch = newSketch(context, id + "F4", { "sketchPlane" : qUnion([Q0])});
            skLineSegment(sketch, "E45.bottom", {"start": v(35, -35) * mm, "end": v(-35, -35) * mm});
            skLineSegment(sketch, "E45.top", {"start": v(35, 35) * mm, "end": v(-35, 35) * mm});
            skLineSegment(sketch, "E45.left", {"start": v(35, -35) * mm, "end": v(35, 35) * mm});
            skLineSegment(sketch, "E45.right", {"start": v(-35, -35) * mm, "end": v(-35, 35) * mm});
            skPoint(sketch, "E45.middle", {"position": v(0, 0) * mm});
            skLineSegment(sketch, "E46.bottom", {"start": v(-55, -15) * mm, "end": v(-15, -15) * mm});
            skLineSegment(sketch, "E46.top", {"start": v(-55, 15) * mm, "end": v(-15, 15) * mm});
            skLineSegment(sketch, "E46.left", {"start": v(-55, -15) * mm, "end": v(-55, 15) * mm});
            skLineSegment(sketch, "E46.right", {"start": v(-15, -15) * mm, "end": v(-15, 15) * mm});
            skPoint(sketch, "E46.middle", {"position": v(-35, 0) * mm});
            skLineSegment(sketch, "E47.bottom", {"start": v(15, -55) * mm, "end": v(-15, -55) * mm});
            skLineSegment(sketch, "E47.top", {"start": v(15, -15) * mm, "end": v(-15, -15) * mm});
            skLineSegment(sketch, "E47.left", {"start": v(15, -55) * mm, "end": v(15, -15) * mm});
            skLineSegment(sketch, "E47.right", {"start": v(-15, -55) * mm, "end": v(-15, -15) * mm});
            skPoint(sketch, "E47.middle", {"position": v(0, -35) * mm});
            skLineSegment(sketch, "E48.bottom", {"start": v(55, 15) * mm, "end": v(15, 15) * mm});
            skLineSegment(sketch, "E48.top", {"start": v(55, -15) * mm, "end": v(15, -15) * mm});
            skLineSegment(sketch, "E48.left", {"start": v(55, 15) * mm, "end": v(55, -15) * mm});
            skLineSegment(sketch, "E48.right", {"start": v(15, 15) * mm, "end": v(15, -15) * mm});
            skPoint(sketch, "E48.middle", {"position": v(35, 0) * mm});
            skLineSegment(sketch, "E49.bottom", {"start": v(15, 55) * mm, "end": v(-15, 55) * mm});
            skLineSegment(sketch, "E49.top", {"start": v(15, 15) * mm, "end": v(-15, 15) * mm});
            skLineSegment(sketch, "E49.left", {"start": v(15, 55) * mm, "end": v(15, 15) * mm});
            skLineSegment(sketch, "E49.right", {"start": v(-15, 55) * mm, "end": v(-15, 15) * mm});
            skPoint(sketch, "E49.middle", {"position": v(0, 35) * mm});
            skSolve(sketch);
        }
        {
            var Q0;
            {var subQ5=sQuery(id+"F4.wireOp",EDGE,"E47.bottom");Q0=makeQuery(id+"F4.imprint","IMPRINT",FACE,{"disambiguationData":[TD([[makeQuery(id+"F4.imprint","IMPRINT",EDGE,{"derivedFrom":subQ5}),-1.0]])]});}
            var Q1;
            {var subQ5=sQuery(id+"F4.wireOp",EDGE,"E48.left");Q1=makeQuery(id+"F4.imprint","IMPRINT",FACE,{"disambiguationData":[TD([[makeQuery(id+"F4.imprint","IMPRINT",EDGE,{"derivedFrom":subQ5}),-1.0]])]});}
            var Q2;
            {var subQ5=sQuery(id+"F4.wireOp",EDGE,"E49.bottom");Q2=makeQuery(id+"F4.imprint","IMPRINT",FACE,{"disambiguationData":[TD([[makeQuery(id+"F4.imprint","IMPRINT",EDGE,{"derivedFrom":subQ5}),1.0]])]});}
            var Q3;
            {var subQ5=sQuery(id+"F4.wireOp",EDGE,"E46.left");Q3=makeQuery(id+"F4.imprint","IMPRINT",FACE,{"disambiguationData":[TD([[makeQuery(id+"F4.imprint","IMPRINT",EDGE,{"derivedFrom":subQ5}),-1.0]])]});}
            extrude(context, id + "F5", {"entities" : qUnion([Q0, Q1, Q2, Q3]), "operationType" : NewBodyOperationType.ADD, "oppositeDirection" : true, "depth" : 9 * mm});
        }
        {
            var Q0;
            Q0=makeQuery(id+"F1.opExtrude","CAP_FACE",FACE,{"disambiguationData":[OSD([sQuery(id+"F0.wireOp",EDGE,"E9"),sQuery(id+"F0.wireOp",EDGE,"E10"),sQuery(id+"F0.wireOp",EDGE,"E11"),sQuery(id+"F0.wireOp",EDGE,"E12"),sQuery(id+"F0.wireOp",EDGE,"E13"),sQuery(id+"F0.wireOp",EDGE,"E14"),sQuery(id+"F0.wireOp",EDGE,"E15"),sQuery(id+"F0.wireOp",EDGE,"E16"),sQuery(id+"F0.wireOp",EDGE,"E18"),sQuery(id+"F0.wireOp",EDGE,"E20"),sQuery(id+"F0.wireOp",EDGE,"E22"),sQuery(id+"F0.wireOp",EDGE,"E24"),sQuery(id+"F0.wireOp",EDGE,"E25"),sQuery(id+"F0.wireOp",EDGE,"E26"),sQuery(id+"F0.wireOp",EDGE,"E30"),sQuery(id+"F0.wireOp",EDGE,"E31"),sQuery(id+"F0.wireOp",EDGE,"E32"),sQuery(id+"F0.wireOp",EDGE,"E36"),sQuery(id+"F0.wireOp",EDGE,"E40"),sQuery(id+"F0.wireOp",EDGE,"E44")])],"isStart":true});
            var sketch = newSketch(context, id + "F6", { "sketchPlane" : qUnion([Q0])});
            skLineSegment(sketch, "E50.bottom", {"start": v(30, 30) * mm, "end": v(-30, 30) * mm});
            skLineSegment(sketch, "E50.top", {"start": v(30, -30) * mm, "end": v(-30, -30) * mm});
            skLineSegment(sketch, "E50.left", {"start": v(30, 30) * mm, "end": v(30, -30) * mm});
            skLineSegment(sketch, "E50.right", {"start": v(-30, 30) * mm, "end": v(-30, -30) * mm});
            skPoint(sketch, "E50.middle", {"position": v(0, 0) * mm});
            skSolve(sketch);
        }
        {
            var Q0;
            Q0 = qSketchRegion(id + "F6", true);
            extrude(context, id + "F7", {"entities" : qUnion([Q0]), "operationType" : NewBodyOperationType.REMOVE, "oppositeDirection" : true, "depth" : 30 * mm});
        }
        {
            var Q0;
            {var subQ0=sQuery(id+"F0.wireOp",EDGE,"E26");Q0=makeQuery(id+"F1.opExtrude","CAP_EDGE",EDGE,{"disambiguationData":[OSD([subQ0]),TDD([makeQuery(id+"F0.imprint","IMPRINT",EDGE,{"disambiguationData":[TD([[makeQuery(id+"F0.imprint","INTERSECT",VERTEX,{"derivedFrom":[subQ0,sQuery(id+"F0.wireOp",EDGE,"E30")]}),-1.0]])],"derivedFrom":subQ0})])],"isStart":false});}
            var Q1;
            {var subQ0=sQuery(id+"F0.wireOp",EDGE,"E25");Q1=makeQuery(id+"F1.opExtrude","CAP_EDGE",EDGE,{"disambiguationData":[OSD([subQ0]),TDD([makeQuery(id+"F0.imprint","IMPRINT",EDGE,{"disambiguationData":[TD([[makeQuery(id+"F0.imprint","INTERSECT",VERTEX,{"derivedFrom":[subQ0,sQuery(id+"F0.wireOp",EDGE,"E30")]}),1.0]])],"derivedFrom":subQ0})])],"isStart":false});}
            var Q2;
            Q2=makeQuery(id+"F1.opExtrude","CAP_EDGE",EDGE,{"disambiguationData":[OSD([sQuery(id+"F0.wireOp",EDGE,"E30")])],"isStart":false});
            var Q3;
            {var subQ0=sQuery(id+"F0.wireOp",EDGE,"E26");Q3=makeQuery(id+"F1.opExtrude","CAP_EDGE",EDGE,{"disambiguationData":[OSD([subQ0]),TDD([makeQuery(id+"F0.imprint","IMPRINT",EDGE,{"disambiguationData":[TD([[makeQuery(id+"F0.imprint","INTERSECT",VERTEX,{"derivedFrom":[subQ0,sQuery(id+"F0.wireOp",EDGE,"E36")]}),1.0]])],"derivedFrom":subQ0})])],"isStart":false});}
            var Q4;
            {var subQ0=sQuery(id+"F0.wireOp",EDGE,"E32");Q4=makeQuery(id+"F1.opExtrude","CAP_EDGE",EDGE,{"disambiguationData":[OSD([subQ0]),TDD([makeQuery(id+"F0.imprint","IMPRINT",EDGE,{"disambiguationData":[TD([[makeQuery(id+"F0.imprint","INTERSECT",VERTEX,{"derivedFrom":[subQ0,sQuery(id+"F0.wireOp",EDGE,"E36")]}),-1.0]])],"derivedFrom":subQ0})])],"isStart":false});}
            var Q5;
            Q5=makeQuery(id+"F1.opExtrude","CAP_EDGE",EDGE,{"disambiguationData":[OSD([sQuery(id+"F0.wireOp",EDGE,"E36")])],"isStart":false});
            var Q6;
            {var subQ0=sQuery(id+"F0.wireOp",EDGE,"E31");Q6=makeQuery(id+"F1.opExtrude","CAP_EDGE",EDGE,{"disambiguationData":[OSD([subQ0]),TDD([makeQuery(id+"F0.imprint","IMPRINT",EDGE,{"disambiguationData":[TD([[makeQuery(id+"F0.imprint","INTERSECT",VERTEX,{"derivedFrom":[subQ0,sQuery(id+"F0.wireOp",EDGE,"E44")]}),-1.0]])],"derivedFrom":subQ0})])],"isStart":false});}
            var Q7;
            {var subQ0=sQuery(id+"F0.wireOp",EDGE,"E32");Q7=makeQuery(id+"F1.opExtrude","CAP_EDGE",EDGE,{"disambiguationData":[OSD([subQ0]),TDD([makeQuery(id+"F0.imprint","IMPRINT",EDGE,{"disambiguationData":[TD([[makeQuery(id+"F0.imprint","INTERSECT",VERTEX,{"derivedFrom":[subQ0,sQuery(id+"F0.wireOp",EDGE,"E44")]}),1.0]])],"derivedFrom":subQ0})])],"isStart":false});}
            var Q8;
            Q8=makeQuery(id+"F1.opExtrude","CAP_EDGE",EDGE,{"disambiguationData":[OSD([sQuery(id+"F0.wireOp",EDGE,"E44")])],"isStart":false});
            var Q9;
            {var subQ0=sQuery(id+"F0.wireOp",EDGE,"E31");Q9=makeQuery(id+"F1.opExtrude","CAP_EDGE",EDGE,{"disambiguationData":[OSD([subQ0]),TDD([makeQuery(id+"F0.imprint","IMPRINT",EDGE,{"disambiguationData":[TD([[makeQuery(id+"F0.imprint","INTERSECT",VERTEX,{"derivedFrom":[subQ0,sQuery(id+"F0.wireOp",EDGE,"E40")]}),1.0]])],"derivedFrom":subQ0})])],"isStart":false});}
            var Q10;
            Q10=makeQuery(id+"F1.opExtrude","CAP_EDGE",EDGE,{"disambiguationData":[OSD([sQuery(id+"F0.wireOp",EDGE,"E40")])],"isStart":false});
            var Q11;
            {var subQ0=sQuery(id+"F0.wireOp",EDGE,"E25");Q11=makeQuery(id+"F1.opExtrude","CAP_EDGE",EDGE,{"disambiguationData":[OSD([subQ0]),TDD([makeQuery(id+"F0.imprint","IMPRINT",EDGE,{"disambiguationData":[TD([[makeQuery(id+"F0.imprint","INTERSECT",VERTEX,{"derivedFrom":[subQ0,sQuery(id+"F0.wireOp",EDGE,"E40")]}),-1.0]])],"derivedFrom":subQ0})])],"isStart":false});}
            fillet(context, id + "F8", {"entities" : qUnion([Q0, Q1, Q2, Q3, Q4, Q5, Q6, Q7, Q8, Q9, Q10, Q11]), "radius" : 5 * mm, "tangentPropagation" : true, "allowEdgeOverflow" : false});
        }
        {
            var Q0;
            {var subQ0=sQuery(id+"F0.wireOp",EDGE,"E25");Q0=makeQuery(id+"F1.opExtrude","CAP_EDGE",EDGE,{"disambiguationData":[OSD([subQ0]),TDD([makeQuery(id+"F0.imprint","IMPRINT",EDGE,{"disambiguationData":[TD([[makeQuery(id+"F0.imprint","INTERSECT",VERTEX,{"derivedFrom":[sQuery(id+"F0.wireOp",EDGE,"E18"),subQ0]}),-1.0]])],"derivedFrom":subQ0})])],"isStart":false});}
            var Q1;
            {var subQ0=sQuery(id+"F0.wireOp",EDGE,"E31");Q1=makeQuery(id+"F1.opExtrude","CAP_EDGE",EDGE,{"disambiguationData":[OSD([subQ0]),TDD([makeQuery(id+"F0.imprint","IMPRINT",EDGE,{"disambiguationData":[TD([[makeQuery(id+"F0.imprint","INTERSECT",VERTEX,{"derivedFrom":[sQuery(id+"F0.wireOp",EDGE,"E20"),subQ0]}),-1.0]])],"derivedFrom":subQ0})])],"isStart":false});}
            var Q2;
            {var subQ0=sQuery(id+"F0.wireOp",EDGE,"E32");Q2=makeQuery(id+"F1.opExtrude","CAP_EDGE",EDGE,{"disambiguationData":[OSD([subQ0]),TDD([makeQuery(id+"F0.imprint","IMPRINT",EDGE,{"disambiguationData":[TD([[makeQuery(id+"F0.imprint","INTERSECT",VERTEX,{"derivedFrom":[sQuery(id+"F0.wireOp",EDGE,"E22"),subQ0]}),-1.0]])],"derivedFrom":subQ0})])],"isStart":false});}
            var Q3;
            {var subQ0=sQuery(id+"F0.wireOp",EDGE,"E26");Q3=makeQuery(id+"F1.opExtrude","CAP_EDGE",EDGE,{"disambiguationData":[OSD([subQ0]),TDD([makeQuery(id+"F0.imprint","IMPRINT",EDGE,{"disambiguationData":[TD([[makeQuery(id+"F0.imprint","INTERSECT",VERTEX,{"derivedFrom":[sQuery(id+"F0.wireOp",EDGE,"E18"),subQ0]}),1.0]])],"derivedFrom":subQ0})])],"isStart":false});}
            fillet(context, id + "F9", {"entities" : qUnion([Q0, Q1, Q2, Q3]), "radius" : 11 * mm, "tangentPropagation" : true, "allowEdgeOverflow" : false});
        }
    });
